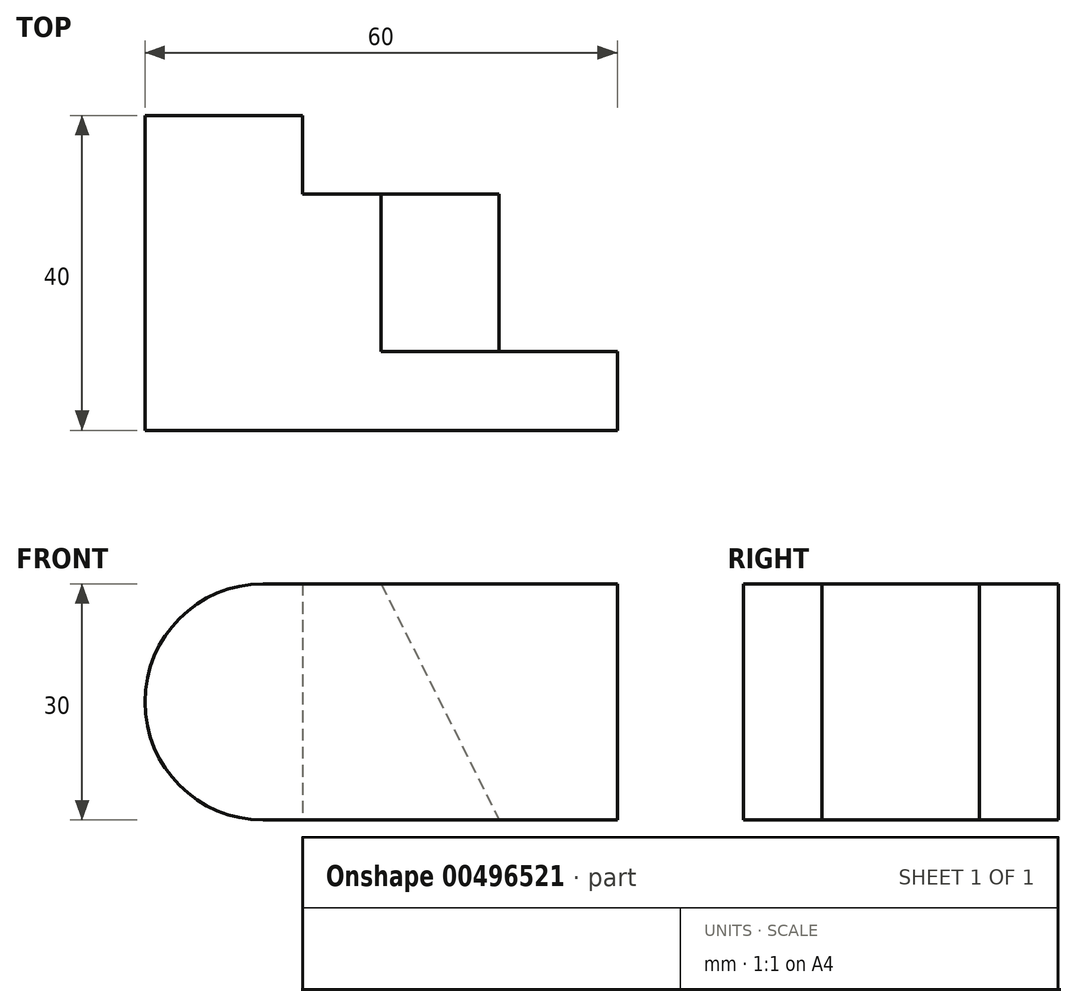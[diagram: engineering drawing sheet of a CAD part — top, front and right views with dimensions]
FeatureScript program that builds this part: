
annotation { "Feature Type Name" : "Feature", "Feature Type Description" : "" }
export const myFeature = defineFeature(function(context is Context, id is Id, definition is map)
    precondition{}
    {
        {
            var Q0;
            Q0=qCreatedBy(makeId("Top.planeOp"),FACE);
            var sketch = newSketch(context, id + "F0", { "sketchPlane" : qUnion([Q0])});
            skLineSegment(sketch, "E0", {"start": v(0, 0) * mm, "end": v(60, 0) * mm});
            skLineSegment(sketch, "E1", {"start": v(60, 0) * mm, "end": v(60, 10) * mm});
            skLineSegment(sketch, "E2", {"start": v(0, 0) * mm, "end": v(0, 40) * mm});
            skLineSegment(sketch, "E3", {"start": v(0, 40) * mm, "end": v(20, 40) * mm});
            skLineSegment(sketch, "E4", {"start": v(20, 40) * mm, "end": v(20, 30) * mm});
            skLineSegment(sketch, "E5", {"start": v(20, 30) * mm, "end": v(30, 30) * mm});
            skLineSegment(sketch, "E6", {"start": v(30, 30) * mm, "end": v(30, 10) * mm});
            skLineSegment(sketch, "E7", {"start": v(30, 10) * mm, "end": v(60, 10) * mm});
            skSolve(sketch);
        }
        {
            var Q0;
            Q0 = qSketchRegion(id + "F0", true);
            extrude(context, id + "F1", {"entities" : qUnion([Q0]), "depth" : 30 * mm, "offsetDistance" : 25 * mm});
        }
        {
            var Q0;
            Q0=makeQuery(id+"F1.opExtrude","CAP_EDGE",EDGE,{"disambiguationData":[OSD([sQuery(id+"F0.wireOp",EDGE,"E2")])],"isStart":false});
            var Q1;
            Q1=makeQuery(id+"F1.opExtrude","CAP_EDGE",EDGE,{"disambiguationData":[OSD([sQuery(id+"F0.wireOp",EDGE,"E2")])],"isStart":true});
            fillet(context, id + "F2", {"entities" : qUnion([Q0, Q1]), "radius" : 15 * mm, "tangentPropagation" : true, "allowEdgeOverflow" : false});
        }
        {
            var Q0;
            Q0=makeQuery(id+"F1.opExtrude","SWEPT_FACE",FACE,{"disambiguationData":[OSD([sQuery(id+"F0.wireOp",EDGE,"E7")])]});
            var sketch = newSketch(context, id + "F3", { "sketchPlane" : qUnion([Q0])});
            skLineSegment(sketch, "E8", {"start": v(-30, 30) * mm, "end": v(-45, 0) * mm});
            skLineSegment(sketch, "E9", {"start": v(-45, 0) * mm, "end": v(-30, 0) * mm});
            skLineSegment(sketch, "E10", {"start": v(-30, 0) * mm, "end": v(-30, 30) * mm});
            skSolve(sketch);
        }
        {
            var Q0;
            Q0 = qSketchRegion(id + "F3", true);
            extrude(context, id + "F4", {"entities" : qUnion([Q0]), "operationType" : NewBodyOperationType.ADD, "depth" : 20 * mm, "offsetDistance" : 25 * mm});
        }
    });
